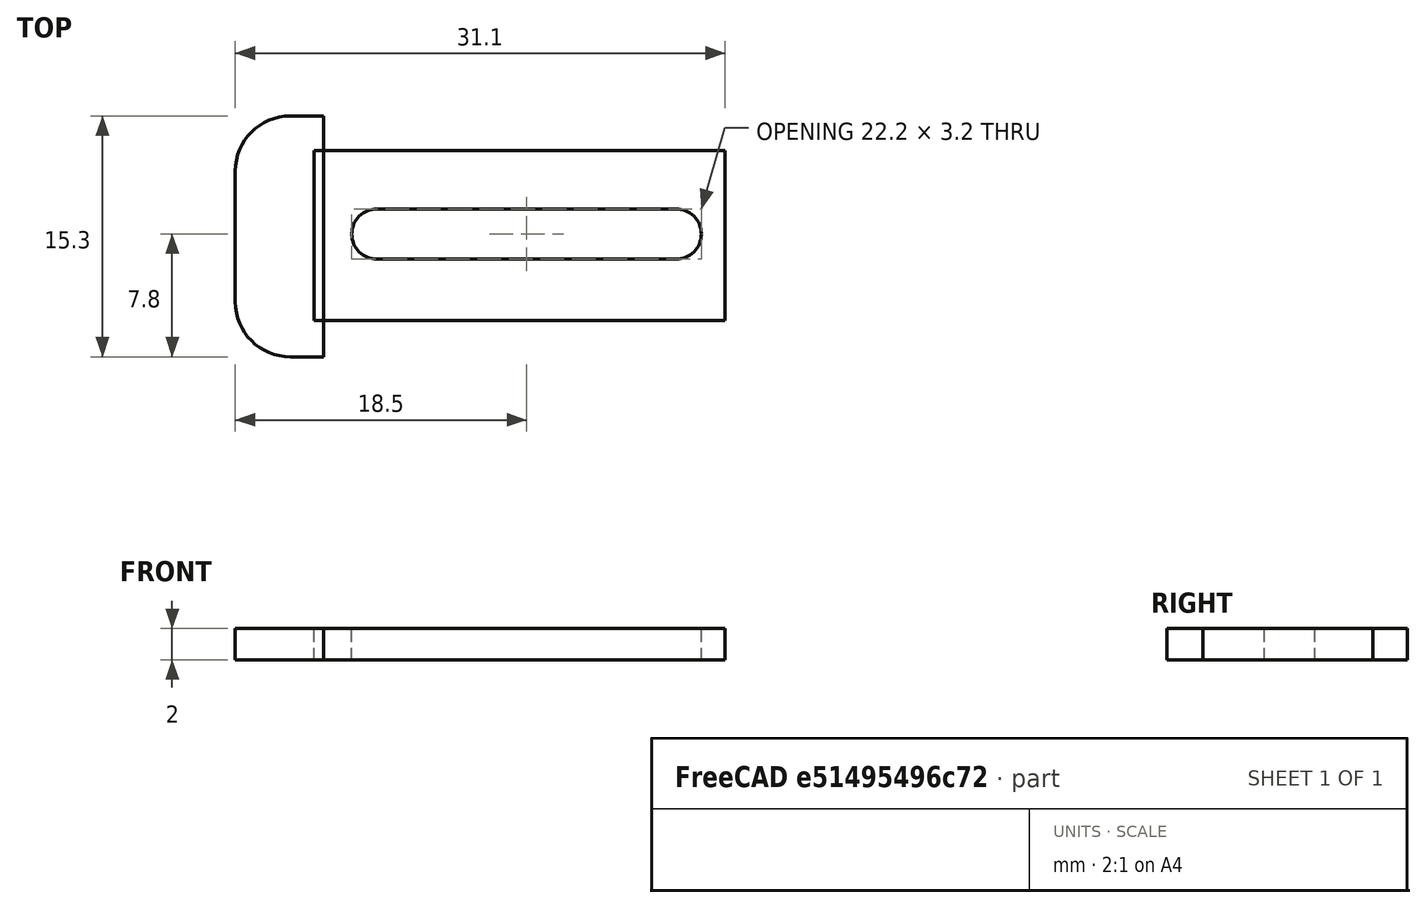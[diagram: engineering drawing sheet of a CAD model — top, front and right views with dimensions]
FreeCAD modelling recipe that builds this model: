
FCSTD DOCUMENT  (FreeCAD 0.17R13522 (Git))
Label: lateral
License: All rights reserved
LicenseURL: http://en.wikipedia.org/wiki/All_rights_reserved
objects: Part::Box×3, Part::Cylinder×2, Part::Fillet×2, Part::MultiFuse×1, Part::Cut×1
note: 9 computed .brp shape members not serialized (recipe doc carries the construction recipe); baked Part::Feature solids carry a one-line shape summary decoded from their .brp

FEATURE [Part::Box] Box  label="Cubo"
  AttacherType = Attacher::AttachEngine3D
  Height = 2
  Length = 5.6
  Placement = pos=(3,-0.3,0) rot=(0,0,1;0rad)
  Width = 15.3
FEATURE [Part::Box] Box001  label="Cubo001"
  AttacherType = Attacher::AttachEngine3D
  Height = 2
  Length = 26.1
  Placement = pos=(8,2,0) rot=(0,0,1;0rad)
  Width = 10.8
FEATURE [Part::Cylinder] Cylinder  label="Cilindro"
  Angle = 360
  AttacherType = Attacher::AttachEngine3D
  Height = 10
  Placement = pos=(12,7.5,-3) rot=(0,0,1;0rad)
  Radius = 1.6
FEATURE [Part::Box] Box002  label="Cubo002"
  AttacherType = Attacher::AttachEngine3D
  Height = 10
  Length = 19
  Placement = pos=(12,5.9,-2) rot=(0,0,1;0rad)
  Width = 3.2
FEATURE [Part::Cylinder] Cylinder001  label="Cilindro001"
  Angle = 360
  AttacherType = Attacher::AttachEngine3D
  Height = 10
  Placement = pos=(31,7.5,-3) rot=(0,0,1;0rad)
  Radius = 1.6
FEATURE [Part::MultiFuse] Fusion
  Shapes = -> [Box002,Cylinder001,Cylinder]
FEATURE [Part::Cut] Cut
  Base = -> Box001
  Tool = -> Fusion
FEATURE [Part::Fillet] Fillet
  Base = -> Box
  Edges = 1 edges r=3.5: [Edge3]
FEATURE [Part::Fillet] Fillet001
  Base = -> Fillet
  Edges = 1 edges r=3.5: [Edge3]
